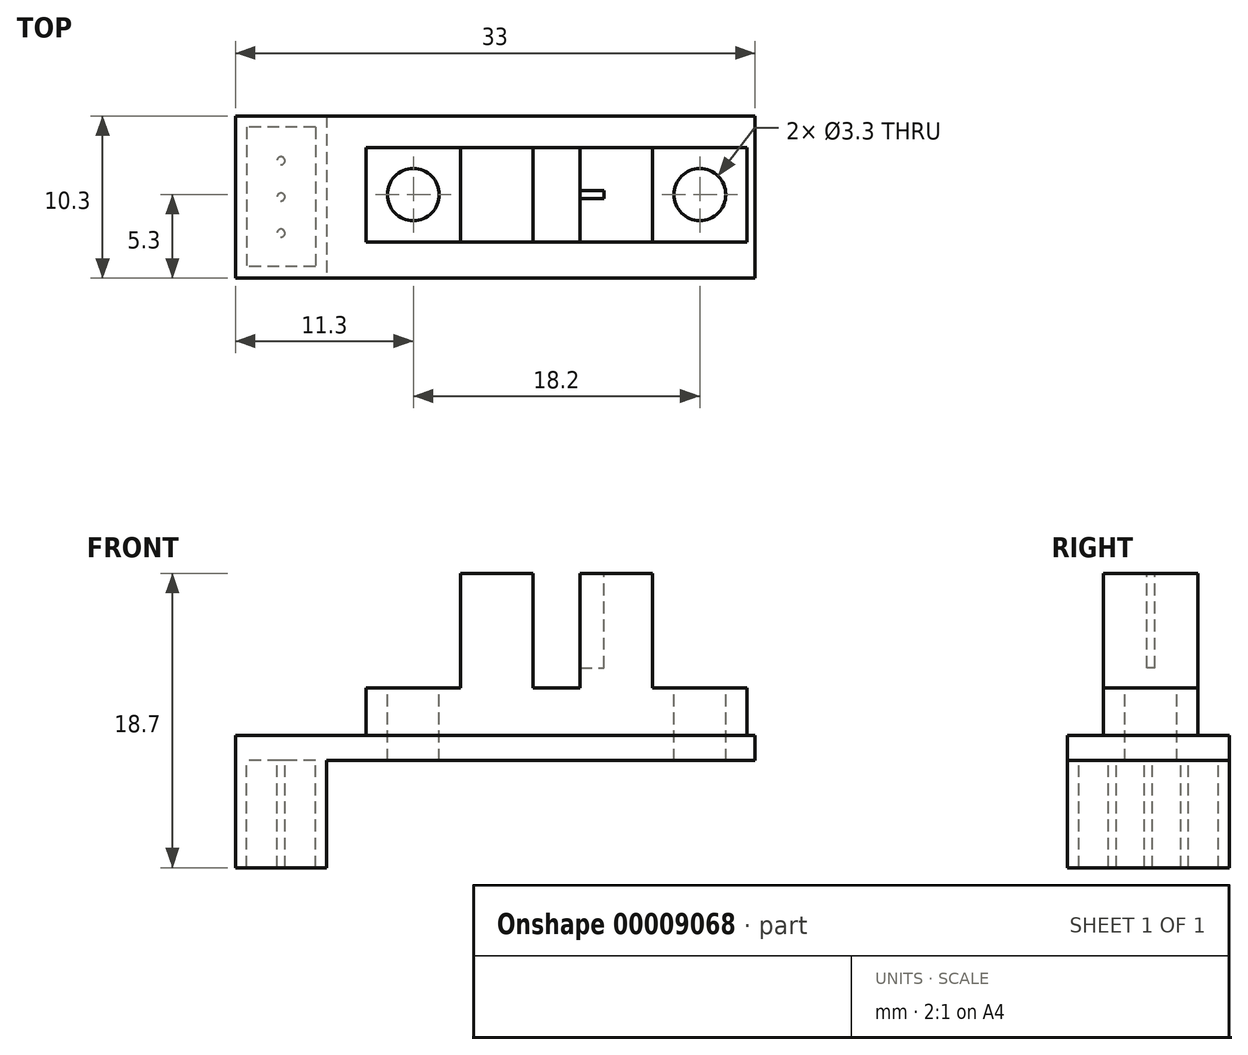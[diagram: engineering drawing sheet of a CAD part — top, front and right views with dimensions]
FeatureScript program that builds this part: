
annotation { "Feature Type Name" : "Feature", "Feature Type Description" : "" }
export const myFeature = defineFeature(function(context is Context, id is Id, definition is map)
    precondition{}
    {
        {
            var Q0;
            Q0=qCreatedBy(makeId("Top.planeOp"),FACE);
            var sketch = newSketch(context, id + "F0", { "sketchPlane" : qUnion([Q0])});
            skLineSegment(sketch, "E0.bottom", {"start": v(16.5, -5.15) * mm, "end": v(-16.5, -5.15) * mm});
            skLineSegment(sketch, "E0.top", {"start": v(16.5, 5.15) * mm, "end": v(-16.5, 5.15) * mm});
            skLineSegment(sketch, "E0.left", {"start": v(16.5, -5.15) * mm, "end": v(16.5, 5.15) * mm});
            skLineSegment(sketch, "E0.right", {"start": v(-16.5, -5.15) * mm, "end": v(-16.5, 5.15) * mm});
            skPoint(sketch, "E0.middle", {"position": v(0, 0) * mm});
            skSolve(sketch);
        }
        {
            var Q0;
            Q0 = qSketchRegion(id + "F0", true);
            extrude(context, id + "F1", {"entities" : qUnion([Q0]), "depth" : 1.6 * mm});
        }
        {
            var Q0;
            Q0=makeQuery(id+"F1.opExtrude","CAP_FACE",FACE,{"disambiguationData":[OSD([sQuery(id+"F0.wireOp",EDGE,"E0.bottom"),sQuery(id+"F0.wireOp",EDGE,"E0.top"),sQuery(id+"F0.wireOp",EDGE,"E0.left"),sQuery(id+"F0.wireOp",EDGE,"E0.right")])],"isStart":false});
            var sketch = newSketch(context, id + "F2", { "sketchPlane" : qUnion([Q0])});
            skLineSegment(sketch, "E1.bottom", {"start": v(-8.2, 3.15) * mm, "end": v(16, 3.15) * mm});
            skLineSegment(sketch, "E1.top", {"start": v(-8.2, -2.85) * mm, "end": v(16, -2.85) * mm});
            skLineSegment(sketch, "E1.left", {"start": v(-8.2, 3.15) * mm, "end": v(-8.2, -2.85) * mm});
            skLineSegment(sketch, "E1.right", {"start": v(16, 3.15) * mm, "end": v(16, -2.85) * mm});
            skLineSegment(sketch, "E2", {"start": v(-2.2, 3.15) * mm, "end": v(-2.2, -2.85) * mm});
            skLineSegment(sketch, "E3", {"start": v(2.4, 3.15) * mm, "end": v(2.4, -2.85) * mm});
            skLineSegment(sketch, "E4", {"start": v(5.4, 3.15) * mm, "end": v(5.4, -2.85) * mm});
            skLineSegment(sketch, "E5", {"start": v(10, 3.15) * mm, "end": v(10, -2.85) * mm});
            skLineSegment(sketch, "E6", {"start": v(2.4, 0) * mm, "end": v(5.4, 0) * mm, "construction": true});
            skPoint(sketch, "E7", {"position": v(3.9, 0) * mm});
            skPoint(sketch, "E8", {"position": v(3.9, 3.15) * mm});
            skSolve(sketch);
        }
        {
            var Q0;
            Q0 = qSketchRegion(id + "F2", true);
            extrude(context, id + "F3", {"entities" : qUnion([Q0]), "operationType" : NewBodyOperationType.ADD, "depth" : 3 * mm});
        }
        {
            var Q0;
            {var subQ0=sQuery(id+"F2.wireOp",EDGE,"E2");Q0=makeQuery(id+"F2.imprint","IMPRINT",FACE,{"disambiguationData":[TD([[makeQuery(id+"F2.imprint","IMPRINT",EDGE,{"derivedFrom":subQ0}),1.0]])]});}
            var Q1;
            {var subQ0=sQuery(id+"F2.wireOp",EDGE,"E4");Q1=makeQuery(id+"F2.imprint","IMPRINT",FACE,{"disambiguationData":[TD([[makeQuery(id+"F2.imprint","IMPRINT",EDGE,{"derivedFrom":subQ0}),1.0]])]});}
            extrude(context, id + "F4", {"entities" : qUnion([Q0, Q1]), "operationType" : NewBodyOperationType.ADD, "depth" : 10.3 * mm});
        }
        {
            var Q0;
            {var subQ0=sQuery(id+"F2.wireOp",EDGE,"E1.left");var subQ2=sQuery(id+"F2.wireOp",EDGE,"E1.bottom");var subQ5=sQuery(id+"F2.wireOp",EDGE,"E1.top");Q0=makeQuery(id+"F4.boolean.opBoolean","SPLIT",FACE,{"disambiguationData":[TD([makeQuery(id+"F3.opExtrude","SWEPT_FACE",FACE,{"disambiguationData":[OSD([subQ0])]})])],"derivedFrom":makeQuery(id+"F3.opExtrude","CAP_FACE",FACE,{"disambiguationData":[OSD([subQ2,subQ5,subQ0,sQuery(id+"F2.wireOp",EDGE,"E1.right")])],"isStart":false})});}
            var sketch = newSketch(context, id + "F5", { "sketchPlane" : qUnion([Q0])});
            skCircle(sketch, "E9", {"center": v(-5.2, 0.15) * mm, "radius": 1.65 * mm});
            skPoint(sketch, "E9.centerSnap0", {"position": v(-8.2, 0.15) * mm});
            skPoint(sketch, "E9.centerSnap1", {"position": v(-5.2, -2.85) * mm});
            skLineSegment(sketch, "E10", {"start": v(3.9, 5.15) * mm, "end": v(3.9, -5.15) * mm, "construction": true});
            skCircle(sketch, "E11.MirrorC", {"center": v(13, 0.15) * mm, "radius": 1.65 * mm});
            skSolve(sketch);
        }
        {
            var Q0;
            Q0 = qSketchRegion(id + "F5", true);
            var Q1;
            Q1=makeQuery(id+"F1.opExtrude","CAP_FACE",FACE,{"disambiguationData":[OSD([sQuery(id+"F0.wireOp",EDGE,"E0.bottom"),sQuery(id+"F0.wireOp",EDGE,"E0.top"),sQuery(id+"F0.wireOp",EDGE,"E0.left"),sQuery(id+"F0.wireOp",EDGE,"E0.right")])],"isStart":true});
            extrude(context, id + "F6", {"entities" : qUnion([Q0]), "operationType" : NewBodyOperationType.REMOVE, "endBound" : BoundingType.UP_TO_SURFACE, "oppositeDirection" : true, "endBoundEntityFace" : qUnion([Q1]), "depth" : 25 * mm});
        }
        {
            var Q0;
            Q0=makeQuery(id+"F4.opExtrude","CAP_FACE",FACE,{"disambiguationData":[OSD([sQuery(id+"F2.wireOp",EDGE,"E1.bottom"),sQuery(id+"F2.wireOp",EDGE,"E1.top"),sQuery(id+"F2.wireOp",EDGE,"E4"),sQuery(id+"F2.wireOp",EDGE,"E5")])],"isStart":false});
            var sketch = newSketch(context, id + "F7", { "sketchPlane" : qUnion([Q0])});
            skLineSegment(sketch, "E12", {"start": v(5.4, 0.15) * mm, "end": v(10, 0.15) * mm, "construction": true});
            skLineSegment(sketch, "E13", {"start": v(5.4, -0.1) * mm, "end": v(6.9, -0.1) * mm});
            skLineSegment(sketch, "E14", {"start": v(6.9, -0.1) * mm, "end": v(6.9, 0.4) * mm});
            skLineSegment(sketch, "E15", {"start": v(6.9, 0.4) * mm, "end": v(5.4, 0.4) * mm});
            skPoint(sketch, "E16", {"position": v(6.9, 0.15) * mm});
            skSolve(sketch);
        }
        {
            var Q0;
            {var subQ0=sQuery(id+"F7.wireOp",EDGE,"E13");Q0=makeQuery(id+"F7.imprint","IMPRINT",FACE,{"disambiguationData":[TD([[makeQuery(id+"F7.imprint","IMPRINT",EDGE,{"derivedFrom":subQ0}),1.0]])]});}
            extrude(context, id + "F8", {"entities" : qUnion([Q0]), "operationType" : NewBodyOperationType.REMOVE, "oppositeDirection" : true, "depth" : 6 * mm});
        }
        {
            var Q0;
            Q0=makeQuery(id+"F0.imprint","IMPRINT",FACE,{"disambiguationData":[TD([[makeQuery(id+"F0.imprint","IMPRINT",EDGE,{"derivedFrom":sQuery(id+"F0.wireOp",EDGE,"E0.bottom")}),-1.0]])]});
            var sketch = newSketch(context, id + "F9", { "sketchPlane" : qUnion([Q0])});
            skLineSegment(sketch, "E17.bottom", {"start": v(-10.7, 5.15) * mm, "end": v(-16.5, 5.15) * mm});
            skLineSegment(sketch, "E17.top", {"start": v(-10.7, -5.15) * mm, "end": v(-16.5, -5.15) * mm});
            skLineSegment(sketch, "E17.left", {"start": v(-10.7, 5.15) * mm, "end": v(-10.7, -5.15) * mm});
            skLineSegment(sketch, "E17.right", {"start": v(-16.5, 5.15) * mm, "end": v(-16.5, -5.15) * mm});
            skLineSegment(sketch, "E18.0", {"start": v(-11.42, 4.43) * mm, "end": v(-11.42, -4.43) * mm});
            skLineSegment(sketch, "E18.1", {"start": v(-11.42, 4.43) * mm, "end": v(-15.78, 4.43) * mm});
            skLineSegment(sketch, "E18.2", {"start": v(-15.78, 4.43) * mm, "end": v(-15.78, -4.43) * mm});
            skLineSegment(sketch, "E18.3", {"start": v(-11.42, -4.43) * mm, "end": v(-15.78, -4.43) * mm});
            skLineSegment(sketch, "E19", {"start": v(-13.6, 4.43) * mm, "end": v(-13.6, -4.43) * mm, "construction": true});
            skLineSegment(sketch, "E20", {"start": v(-11.42, 0) * mm, "end": v(-15.78, 0) * mm, "construction": true});
            skCircle(sketch, "E21", {"center": v(-13.6, 0) * mm, "radius": 0.25 * mm});
            skCircle(sketch, "E22", {"center": v(-13.6, -2.3) * mm, "radius": 0.25 * mm});
            skCircle(sketch, "E23", {"center": v(-13.6, 2.3) * mm, "radius": 0.25 * mm});
            skSolve(sketch);
        }
        {
            var Q0;
            Q0=makeQuery(id+"F9.imprint","IMPRINT",FACE,{"disambiguationData":[TD([[makeQuery(id+"F9.imprint","IMPRINT",EDGE,{"derivedFrom":sQuery(id+"F9.wireOp",EDGE,"E17.bottom")}),1.0]])]});
            var Q1;
            Q1=makeQuery(id+"F9.imprint","IMPRINT",FACE,{"disambiguationData":[TD([[makeQuery(id+"F9.imprint","IMPRINT",EDGE,{"derivedFrom":sQuery(id+"F9.wireOp",EDGE,"E21")}),1.0]])]});
            var Q2;
            Q2=makeQuery(id+"F9.imprint","IMPRINT",FACE,{"disambiguationData":[TD([[makeQuery(id+"F9.imprint","IMPRINT",EDGE,{"derivedFrom":sQuery(id+"F9.wireOp",EDGE,"E22")}),1.0]])]});
            var Q3;
            Q3=makeQuery(id+"F9.imprint","IMPRINT",FACE,{"disambiguationData":[TD([[makeQuery(id+"F9.imprint","IMPRINT",EDGE,{"derivedFrom":sQuery(id+"F9.wireOp",EDGE,"E23")}),1.0]])]});
            extrude(context, id + "F10", {"entities" : qUnion([Q0, Q1, Q2, Q3]), "operationType" : NewBodyOperationType.ADD, "oppositeDirection" : true, "depth" : 6.8 * mm});
        }
    });
